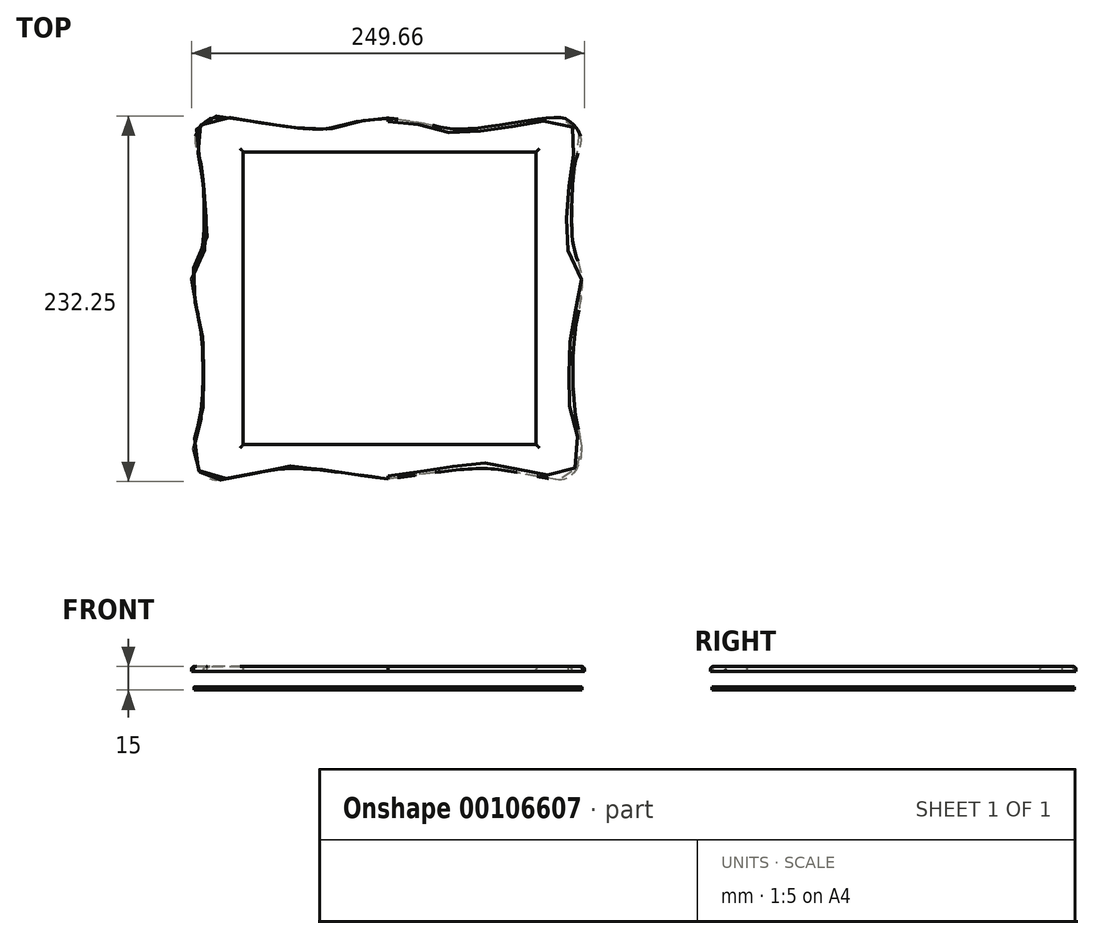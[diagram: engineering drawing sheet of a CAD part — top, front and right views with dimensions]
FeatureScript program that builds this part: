
annotation { "Feature Type Name" : "Feature", "Feature Type Description" : "" }
export const myFeature = defineFeature(function(context is Context, id is Id, definition is map)
    precondition{}
    {
        {
            var Q0;
            Q0=qCreatedBy(makeId("Top.planeOp"),FACE);
            var sketch = newSketch(context, id + "F0", { "sketchPlane" : qUnion([Q0])});
            skLineSegment(sketch, "E0.bottom", {"start": v(-122.5, 118.1) * mm, "end": v(122.5, 118.1) * mm, "construction": true});
            skLineSegment(sketch, "E0.top", {"start": v(-122.5, -111.11) * mm, "end": v(122.5, -111.11) * mm, "construction": true});
            skLineSegment(sketch, "E0.left", {"start": v(-122.5, 118.1) * mm, "end": v(-122.5, -111.11) * mm, "construction": true});
            skLineSegment(sketch, "E0.right", {"start": v(122.5, 118.1) * mm, "end": v(122.5, -111.11) * mm, "construction": true});
            skFitSpline(sketch, "E1", {"points": [v(0, 118.1) * mm, v(20.88, 115.2) * mm, v(36.99, 111.75) * mm, v(45.47, 111.22) * mm, v(51.55, 111.37) * mm, v(59.29, 112.14) * mm, v(75.33, 114.44) * mm, v(99.86, 118.1) * mm, v(111.75, 118.1) * mm, v(117.88, 114.06) * mm, v(122.5, 105.24) * mm, v(119.42, 91.82) * mm, v(117.12, 71.88) * mm, v(117.88, 37) * mm, v(122.5, 20.89) * mm, v(122.5, 3.5) * mm, v(119.03, -16.3) * mm, v(117.5, -40.46) * mm, v(119.03, -69.6) * mm, v(122.5, -87.23) * mm, v(122.5, -97.2) * mm, v(119.42, -105.25) * mm, v(112.52, -111.11) * mm, v(104.08, -111.11) * mm, v(84.91, -107.55) * mm, v(62.3, -104.48) * mm, v(31.62, -106.78) * mm, v(17.8, -108.62) * mm, v(0, -111.11) * mm], "startDerivative": vector(493.95, -54.97) * mm, "endDerivative": vector(-585.5, -82.83) * mm});
            skFitSpline(sketch, "E2.MirrorCS", {"points": [v(0, 118.1) * mm, v(-20.88, 115.2) * mm, v(-36.99, 111.75) * mm, v(-45.47, 111.22) * mm, v(-51.55, 111.37) * mm, v(-59.29, 112.14) * mm, v(-75.33, 114.44) * mm, v(-99.86, 118.1) * mm, v(-111.75, 118.1) * mm, v(-117.88, 114.06) * mm, v(-122.5, 105.24) * mm, v(-119.42, 91.82) * mm, v(-117.12, 71.88) * mm, v(-117.88, 37) * mm, v(-122.5, 20.89) * mm, v(-122.5, 3.5) * mm, v(-119.03, -16.3) * mm, v(-117.5, -40.46) * mm, v(-119.03, -69.6) * mm, v(-122.5, -87.23) * mm, v(-122.5, -97.2) * mm, v(-119.42, -105.25) * mm, v(-112.52, -111.11) * mm, v(-104.08, -111.11) * mm, v(-84.91, -107.55) * mm, v(-62.3, -104.48) * mm, v(-31.62, -106.78) * mm, v(-17.8, -108.62) * mm, v(0, -111.11) * mm], "startDerivative": vector(-493.95, -54.97) * mm, "endDerivative": vector(585.5, -82.83) * mm});
            skSolve(sketch);
        }
        {
            var Q0;
            Q0=makeQuery(id+"F0.imprint","IMPRINT",FACE,{"disambiguationData":[TD([[makeQuery(id+"F0.imprint","IMPRINT",EDGE,{"derivedFrom":sQuery(id+"F0.wireOp",EDGE,"E1")}),-1.0]])]});
            extrude(context, id + "F1", {"entities" : qUnion([Q0]), "depth" : 2 * mm});
        }
        {
            var Q0;
            Q0=makeQuery(id+"F1.opExtrude","CAP_FACE",FACE,{"disambiguationData":[OSD([sQuery(id+"F0.wireOp",EDGE,"E1"),sQuery(id+"F0.wireOp",EDGE,"E2.MirrorCS")])],"isStart":false});
            cPlane(context, id + "F2", {"entities" : qUnion([Q0]), "cplaneType" : CPlaneType.OFFSET, "offset" : 10 * mm, "width" : 150 * mm, "height" : 150 * mm});
        }
        {
            var Q0;
            Q0=qCreatedBy(id+"F2.planeOp",FACE);
            var sketch = newSketch(context, id + "F3", { "sketchPlane" : qUnion([Q0])});
            skFitSpline(sketch, "E3.0.0", {"points": [v(0, -111.11) * mm, v(7.44, -110.06) * mm, v(17.73, -108.63) * mm, v(31.7, -106.71) * mm, v(63, -103) * mm, v(83.84, -107.42) * mm, v(103.65, -111.14) * mm, v(112.63, -112.41) * mm, v(120.18, -105.53) * mm, v(123, -97.14) * mm, v(123.05, -86.58) * mm, v(117.91, -69.16) * mm, v(117.16, -40.36) * mm, v(118.29, -16.58) * mm, v(123.07, 3) * mm, v(123.82, 21.64) * mm, v(115.75, 36.55) * mm, v(117.02, 72.12) * mm, v(118.13, 91.04) * mm, v(124.7, 105.08) * mm, v(118.21, 114.4) * mm, v(111.75, 119.18) * mm, v(99.23, 118.3) * mm, v(75.58, 114.4) * mm, v(59.86, 112.14) * mm, v(51.7, 111.28) * mm, v(45.3, 111.18) * mm, v(36.45, 111.31) * mm, v(20.57, 115.82) * mm, v(6.8, 117.34) * mm, v(0, 118.1) * mm]});
            skFitSpline(sketch, "E3.0.1", {"points": [v(0, 118.1) * mm, v(-6.8, 117.34) * mm, v(-20.57, 115.82) * mm, v(-36.45, 111.31) * mm, v(-45.3, 111.18) * mm, v(-51.7, 111.28) * mm, v(-59.86, 112.14) * mm, v(-75.58, 114.4) * mm, v(-99.23, 118.3) * mm, v(-111.75, 119.18) * mm, v(-118.21, 114.4) * mm, v(-124.7, 105.08) * mm, v(-118.13, 91.04) * mm, v(-117.02, 72.12) * mm, v(-115.75, 36.55) * mm, v(-123.82, 21.64) * mm, v(-123.07, 3) * mm, v(-118.29, -16.58) * mm, v(-117.16, -40.36) * mm, v(-117.91, -69.16) * mm, v(-123.05, -86.58) * mm, v(-123, -97.14) * mm, v(-120.18, -105.53) * mm, v(-112.63, -112.41) * mm, v(-103.65, -111.14) * mm, v(-83.84, -107.42) * mm, v(-63, -103) * mm, v(-31.7, -106.71) * mm, v(-17.73, -108.63) * mm, v(-7.44, -110.06) * mm, v(0, -111.11) * mm]});
            skSolve(sketch);
        }
        {
            var Q0;
            Q0=makeQuery(id+"F3.imprint","IMPRINT",FACE,{"disambiguationData":[TD([[makeQuery(id+"F3.imprint","IMPRINT",EDGE,{"derivedFrom":sQuery(id+"F3.wireOp",EDGE,"E3.0.0")}),1.0]])]});
            extrude(context, id + "F4", {"entities" : qUnion([Q0]), "depth" : 3 * mm});
        }
        {
            var Q0;
            Q0=qCreatedBy(id+"F2.planeOp",FACE);
            cPlane(context, id + "F5", {"entities" : qUnion([Q0]), "cplaneType" : CPlaneType.OFFSET, "offset" : 5 * mm, "width" : 150 * mm, "height" : 150 * mm});
        }
        {
            var Q0;
            Q0=qCreatedBy(id+"F5.planeOp",FACE);
            var sketch = newSketch(context, id + "F6", { "sketchPlane" : qUnion([Q0])});
            skLineSegment(sketch, "E4.0", {"start": v(-91.85, 96.66) * mm, "end": v(94.15, 96.66) * mm});
            skLineSegment(sketch, "E5.0", {"start": v(-91.85, 96.66) * mm, "end": v(-91.85, -89.34) * mm});
            skLineSegment(sketch, "E6.0", {"start": v(-91.85, -89.34) * mm, "end": v(94.15, -89.34) * mm});
            skLineSegment(sketch, "E7.0", {"start": v(94.15, 96.66) * mm, "end": v(94.15, -89.34) * mm});
            skSolve(sketch);
        }
        {
            var Q0;
            Q0 = qSketchRegion(id + "F6", true);
            extrude(context, id + "F7", {"entities" : qUnion([Q0]), "operationType" : NewBodyOperationType.REMOVE, "oppositeDirection" : true, "depth" : 10.5 * mm});
        }
        {
            var Q0;
            Q0=makeQuery(id+"F4.opExtrude","CAP_FACE",FACE,{"disambiguationData":[OSD([sQuery(id+"F3.wireOp",EDGE,"E3.0.0"),sQuery(id+"F3.wireOp",EDGE,"E3.0.1")])],"isStart":false});
            fillet(context, id + "F8", {"entities" : qUnion([Q0]), "radius" : 2 * mm, "tangentPropagation" : true, "allowEdgeOverflow" : false});
        }
    });
